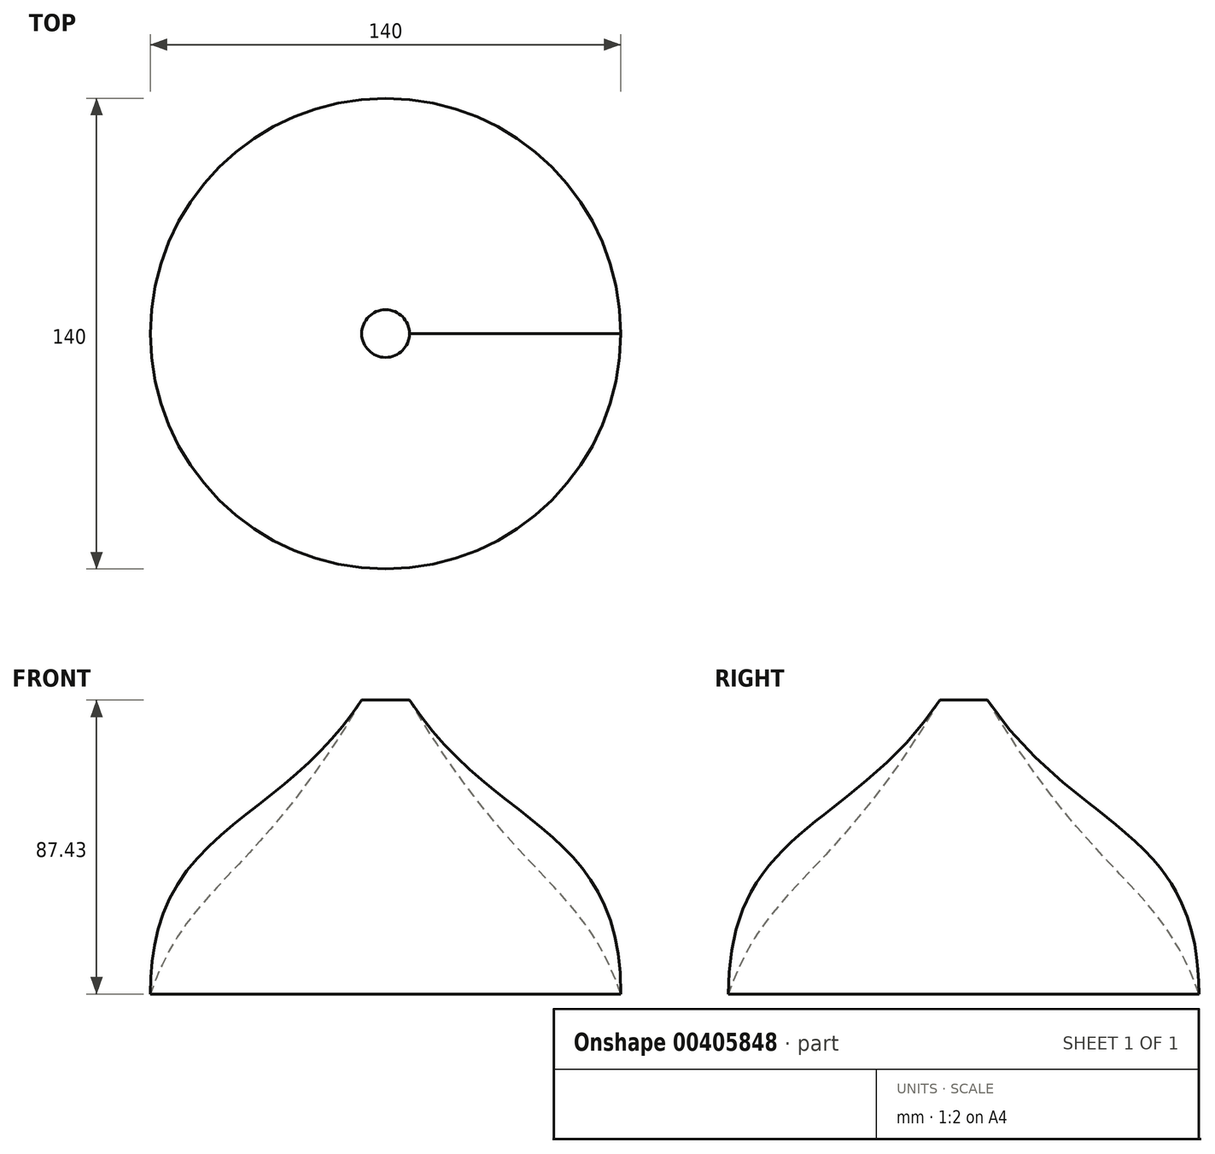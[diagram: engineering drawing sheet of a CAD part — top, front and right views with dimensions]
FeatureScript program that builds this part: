
annotation { "Feature Type Name" : "Feature", "Feature Type Description" : "" }
export const myFeature = defineFeature(function(context is Context, id is Id, definition is map)
    precondition{}
    {
        {
            var Q0;
            Q0=qCreatedBy(makeId("Right.planeOp"),FACE);
            var sketch = newSketch(context, id + "F0", { "sketchPlane" : qUnion([Q0])});
            skLineSegment(sketch, "E0", {"start": v(0, 0) * mm, "end": v(0, 100) * mm});
            skLineSegment(sketch, "E1", {"start": v(0, 0) * mm, "end": v(-70, 0) * mm});
            skFitSpline(sketch, "E2", {"points": [v(0, 100) * mm, v(-70, 0) * mm], "startDerivative": vector(-74.88, -156) * mm, "endDerivative": vector(0, -165) * mm});
            skLineSegment(sketch, "E3", {"start": v(0, 100) * mm, "end": v(-48, 0) * mm});
            skSolve(sketch);
        }
        {
            var Q0;
            {var subQ0=sQuery(id+"F0.wireOp",EDGE,"E2");Q0=makeQuery(id+"F0.imprint","IMPRINT",FACE,{"disambiguationData":[TD([[makeQuery(id+"F0.imprint","IMPRINT",EDGE,{"derivedFrom":subQ0}),1.0]])]});}
            var Q1;
            {var subQ0=sQuery(id+"F0.wireOp",EDGE,"E0");Q1=makeQuery(id+"F0.imprint","IMPRINT",FACE,{"disambiguationData":[TD([[makeQuery(id+"F0.imprint","IMPRINT",EDGE,{"derivedFrom":subQ0}),1.0]])]});}
            var Q2;
            Q2=sQuery(id+"F0.wireOp",EDGE,"E0");
            revolve(context, id + "F1", {"entities" : qUnion([Q0, Q1]), "axis" : qUnion([Q2]), "revolveType" : RevolveType.FULL});
        }
        {
            var Q0;
            Q0=qCreatedBy(makeId("Right.planeOp"),FACE);
            var sketch = newSketch(context, id + "F2", { "sketchPlane" : qUnion([Q0])});
            skPoint(sketch, "E4.0", {"position": v(0, 100) * mm});
            skPoint(sketch, "E5.0", {"position": v(-70, 0) * mm});
            skPoint(sketch, "E6.0", {"position": v(-41.6, 53.32) * mm});
            skFitSpline(sketch, "E7", {"points": [v(-70, 0) * mm, v(0, 100) * mm], "startDerivative": vector(37.44, 108.25) * mm, "endDerivative": vector(109.1, 201.52) * mm});
            skLineSegment(sketch, "E8", {"start": v(-70, 0) * mm, "end": v(0, 0) * mm});
            skLineSegment(sketch, "E9", {"start": v(0, 0) * mm, "end": v(0, 100) * mm});
            skSolve(sketch);
        }
        {
            var Q0;
            Q0 = qSketchRegion(id + "F2", true);
            var Q1;
            Q1=sQuery(id+"F2.wireOp",EDGE,"E9");
            revolve(context, id + "F3", {"operationType" : NewBodyOperationType.REMOVE, "entities" : qUnion([Q0]), "axis" : qUnion([Q1]), "revolveType" : RevolveType.FULL, "oppositeDirection" : true});
        }
    });
